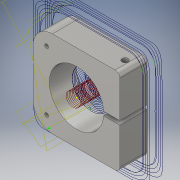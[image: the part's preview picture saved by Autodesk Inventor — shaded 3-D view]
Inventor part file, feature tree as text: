
AUTODESK INVENTOR PART (.ipt)
format: ipt  version: 2016 (Build 200138000, 138)  size: 315,904 bytes
history: native  units: in
note: dims shown in document units (in); Inventor stores cm internally (conversion verified against a paired STEP export)
features: sketch x6, extrude x2, hole x2, projected_geometry x2
ambient origin geometry x8: Origin, YZ Plane, XZ Plane, XY Plane, X Axis, Y Axis, Z Axis, Center Point
bodies: Solid1 (feature_tree)
feature tree (12):
  extrude  "Extrusion1"  Depth=2.25in
  hole  "Hole1"  [1 undecoded]
  hole  "Hole2"  [1 undecoded]
  sketch  "Sketch4"  dims[d8=1.125in d11=2.25in]
  sketch  "Sketch5"  dims[d12=0.7in d13=0.0in]
  extrude  "Extrusion2"  Depth=2.25in
  sketch  "Sketch1"  dims[d0=2.25in d1=2.25in]
  sketch  "Sketch2"  dims[d2=0.5in d3=0.125in]
  projected_geometry  "Projected Loop1"
  sketch  "Sketch3"  dims[d5=0.4in d6=0.408in]
  sketch  "Sketch6"  dims[d14=0.1in d15=0.1in d16=0.1in d17=0.75in d18=0.375in d19=0.25in d20=0.5635in d21=1.0in d22=0.8108in d23=1.415in d24=0.16in d25=0.75in d26=0.3in d27=0.25in d28=0.5635in d29=1.0in d30=0.8108in d31=0.1in d32=0.15in d33=0.15in d34=0.1in d35=0.15in d36=0.15in d37=1.0in d38=0.0in]
  projected_geometry  "Projected Loop2"
note: 2 required parameter values undecoded (feature->parameter linkage not recoverable at this tier; creation-order binding heuristic only, values carry confidence <= 0.55)
